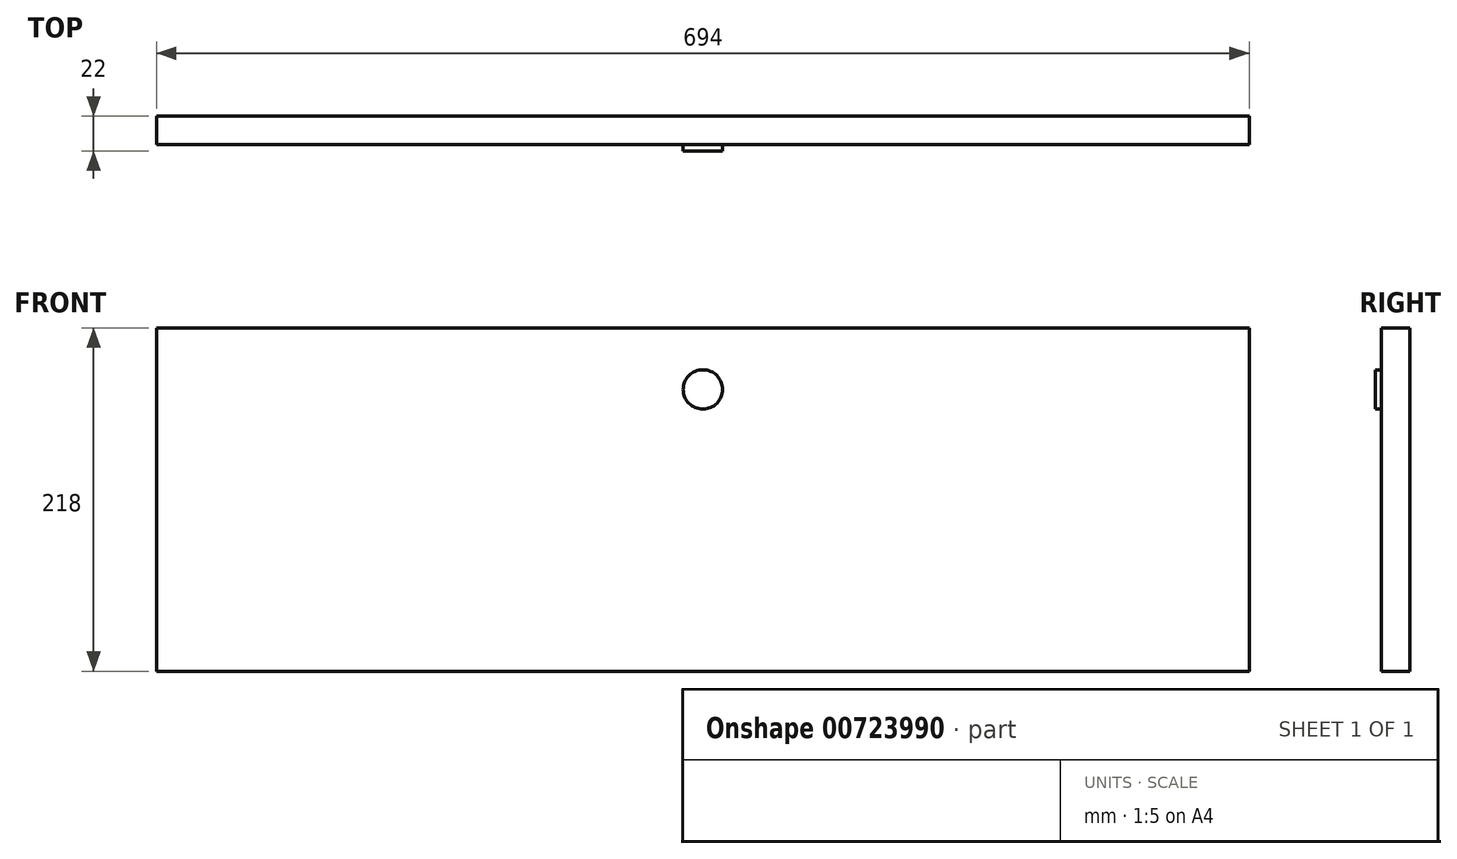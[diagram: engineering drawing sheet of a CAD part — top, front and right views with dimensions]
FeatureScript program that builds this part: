
annotation { "Feature Type Name" : "Feature", "Feature Type Description" : "" }
export const myFeature = defineFeature(function(context is Context, id is Id, definition is map)
    precondition{}
    {
        {
            var Q0;
            Q0=qCreatedBy(makeId("Front.planeOp"),FACE);
            var sketch = newSketch(context, id + "F0", { "sketchPlane" : qUnion([Q0])});
            skLineSegment(sketch, "E0.bottom", {"start": v(-347, 109) * mm, "end": v(347, 109) * mm});
            skLineSegment(sketch, "E0.top", {"start": v(-347, -109) * mm, "end": v(347, -109) * mm});
            skLineSegment(sketch, "E0.left", {"start": v(-347, 109) * mm, "end": v(-347, -109) * mm});
            skLineSegment(sketch, "E0.right", {"start": v(347, 109) * mm, "end": v(347, -109) * mm});
            skLineSegment(sketch, "E1", {"start": v(-347, 109) * mm, "end": v(347, -109) * mm, "construction": true});
            skLineSegment(sketch, "E2", {"start": v(347, 109) * mm, "end": v(-347, -109) * mm, "construction": true});
            skSolve(sketch);
        }
        {
            var Q0;
            Q0=qSketchRegion(id+"F0",true);
            extrude(context, id + "F1", {"entities" : qUnion([Q0]), "depth" : 18 * mm, "offsetDistance" : 25 * mm});
        }
        {
            var Q0;
            Q0=makeQuery(id+"F1.opExtrude","CAP_FACE",FACE,{"disambiguationData":[OSD([sQuery(id+"F0.wireOp",EDGE,"E0.bottom"),sQuery(id+"F0.wireOp",EDGE,"E0.top"),sQuery(id+"F0.wireOp",EDGE,"E0.left"),sQuery(id+"F0.wireOp",EDGE,"E0.right")])],"isStart":false});
            var sketch = newSketch(context, id + "F2", { "sketchPlane" : qUnion([Q0])});
            skCircle(sketch, "E3", {"center": v(0, 70) * mm, "radius": 12.5 * mm});
            skLineSegment(sketch, "E4", {"start": v(0, 70) * mm, "end": v(0, 0) * mm, "construction": true});
            skSolve(sketch);
        }
        {
            var Q0;
            Q0=qSketchRegion(id+"F2",true);
            extrude(context, id + "F3", {"entities" : qUnion([Q0]), "operationType" : NewBodyOperationType.ADD, "depth" : 4 * mm, "offsetDistance" : 25 * mm});
        }
    });
